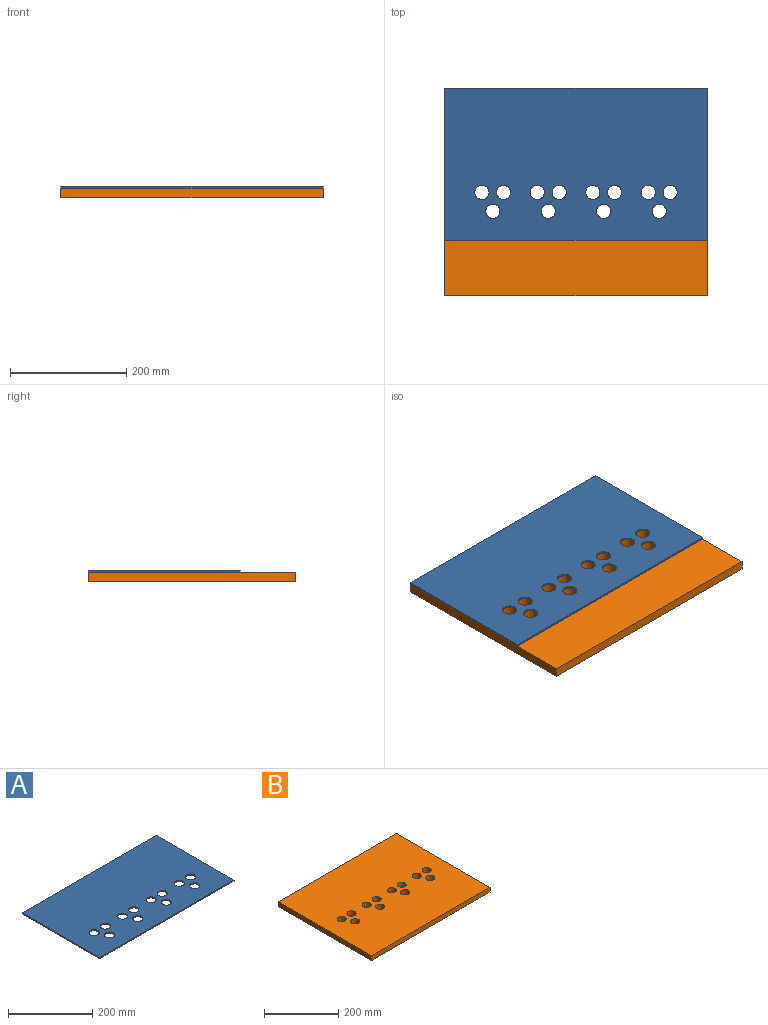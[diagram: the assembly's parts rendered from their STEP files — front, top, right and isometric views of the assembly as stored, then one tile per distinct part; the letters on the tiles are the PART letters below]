
ASSEMBLY  parts=2 mates=1
PART A: 18 faces, bbox 450.9x260.4x3.2 mm
  f0: plane 450.85x260.35mm, normal (0,0,1), area 111775mm2, adj f2,f3,f4,f5,f6,f7,f8,f9
  f1: plane 450.85x260.35mm, normal (0,0,-1), area 111775mm2, adj f2,f3,f4,f5,f6,f7,f8,f9
  f2: plane 450.85x3.18mm, normal (0,1,0), area 1431.4mm2, adj f0,f1,f3,f4
  f3: plane 260.35x3.18mm, normal (-1,0,0), area 826.6mm2, adj f0,f1,f2,f17
  f4: plane 260.35x3.18mm, normal (1,0,0), area 826.6mm2, adj f0,f1,f2,f17
  f5: cylinder r=12.19mm len=24.38mm, axis (0,0,1), area 243.2mm2, adj f0,f1
  f6: cylinder r=12.19mm len=24.38mm, axis (0,0,1), area 243.2mm2, adj f0,f1
  f7: cylinder r=12.19mm len=24.38mm, axis (0,0,1), area 243.2mm2, adj f0,f1
  f8: cylinder r=12.19mm len=24.38mm, axis (0,0,1), area 243.2mm2, adj f0,f1
  f9: cylinder r=12.19mm len=24.38mm, axis (0,0,1), area 243.2mm2, adj f0,f1
  f10: cylinder r=12.19mm len=24.38mm, axis (0,0,1), area 243.2mm2, adj f0,f1
  f11: cylinder r=12.19mm len=24.38mm, axis (0,0,1), area 243.2mm2, adj f0,f1
  f12: cylinder r=12.19mm len=24.38mm, axis (0,0,1), area 243.2mm2, adj f0,f1
  f13: cylinder r=12.19mm len=24.38mm, axis (0,0,1), area 243.2mm2, adj f0,f1
  f14: cylinder r=12.19mm len=24.38mm, axis (0,0,1), area 243.2mm2, adj f0,f1
  f15: cylinder r=12.19mm len=24.38mm, axis (0,0,1), area 243.2mm2, adj f0,f1
  f16: cylinder r=12.19mm len=24.38mm, axis (0,0,1), area 243.2mm2, adj f0,f1
  f17: plane 450.85x3.18mm, normal (0,-1,0), area 1431.4mm2, adj f0,f1,f3,f4
PART B: 18 faces, bbox 450.9x355.6x15.9 mm
  f0: plane 450.85x15.88mm, normal (0,1,0), area 7157.2mm2, adj f1,f3,f4,f5
  f1: plane 355.6x15.88mm, normal (-1,0,0), area 5645.2mm2, adj f0,f2,f4,f5
  f2: plane 450.85x15.88mm, normal (0,-1,0), area 7157.2mm2, adj f1,f3,f4,f5
  f3: plane 355.6x15.88mm, normal (1,0,0), area 5645.2mm2, adj f0,f2,f4,f5
  f4: plane 450.85x355.6mm, normal (0,0,1), area 154718.5mm2, adj f0,f1,f2,f3,f6,f7,f8,f9
  f5: plane 450.85x355.6mm, normal (0,0,-1), area 154718.5mm2, adj f0,f1,f2,f3,f6,f7,f8,f9
  f6: cylinder r=12.19mm len=24.38mm, axis (0,0,1), area 1216.1mm2, adj f4,f5
  f7: cylinder r=12.19mm len=24.38mm, axis (0,0,1), area 1216.1mm2, adj f4,f5
  f8: cylinder r=12.19mm len=24.38mm, axis (0,0,1), area 1216.1mm2, adj f4,f5
  f9: cylinder r=12.19mm len=24.38mm, axis (0,0,1), area 1216.1mm2, adj f4,f5
  f10: cylinder r=12.19mm len=24.38mm, axis (0,0,1), area 1216.1mm2, adj f4,f5
  f11: cylinder r=12.19mm len=24.38mm, axis (0,0,1), area 1216.1mm2, adj f4,f5
  f12: cylinder r=12.19mm len=24.38mm, axis (0,0,1), area 1216.1mm2, adj f4,f5
  f13: cylinder r=12.19mm len=24.38mm, axis (0,0,1), area 1216.1mm2, adj f4,f5
  f14: cylinder r=12.19mm len=24.38mm, axis (0,0,1), area 1216.1mm2, adj f4,f5
  f15: cylinder r=12.19mm len=24.38mm, axis (0,0,1), area 1216.1mm2, adj f4,f5
  f16: cylinder r=12.19mm len=24.38mm, axis (0,0,1), area 1216.1mm2, adj f4,f5
  f17: cylinder r=12.19mm len=24.38mm, axis (0,0,1), area 1216.1mm2, adj f4,f5
PLACE A t=(-225.21,176.99,-14.66)mm
PLACE B t=(-225.21,176.99,-14.66)mm fixed
MATE fastened B.f4 <-> A.f1  axis (0,0,1) through (0.22,354.79,1.21)mm
